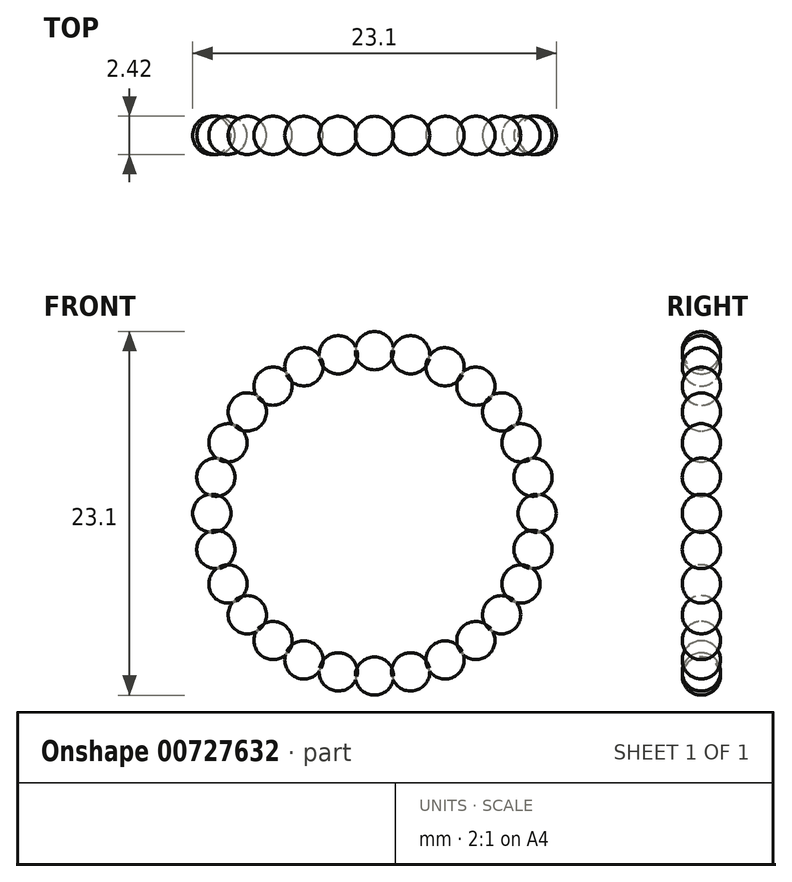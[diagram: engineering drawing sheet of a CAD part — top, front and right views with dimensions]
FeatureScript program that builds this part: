
annotation { "Feature Type Name" : "Feature", "Feature Type Description" : "" }
export const myFeature = defineFeature(function(context is Context, id is Id, definition is map)
    precondition{}
    {
        {
            var Q0;
            Q0=qCreatedBy(makeId("Front.planeOp"),FACE);
            var sketch = newSketch(context, id + "F0", { "sketchPlane" : qUnion([Q0])});
            skCircle(sketch, "E0", {"center": v(0, 0) * mm, "radius": 9.5 * mm});
            skCircle(sketch, "E1", {"center": v(10.33, 0) * mm, "radius": 1.21 * mm});
            skLineSegment(sketch, "E2", {"start": v(10.33, 2.28) * mm, "end": v(10.33, -2.1) * mm});
            skSolve(sketch);
        }
        {
            var Q0;
            {var subQ0=sQuery(id+"F0.wireOp",EDGE,"E2");var subQ1=sQuery(id+"F0.wireOp",EDGE,"E1");var subQ2=makeQuery(id+"F0.imprint","INTERSECT",VERTEX,{"disambiguationData":[OD(0.0)],"derivedFrom":[subQ1,subQ0]});Q0=makeQuery(id+"F0.imprint","IMPRINT",FACE,{"disambiguationData":[TD([[makeQuery(id+"F0.imprint","IMPRINT",EDGE,{"disambiguationData":[TD([[subQ2,1.0]])],"derivedFrom":subQ1}),1.0]])]});}
            var Q1;
            Q1=sQuery(id+"F0.wireOp",EDGE,"E2");
            revolve(context, id + "F1", {"surfaceOperationType" : NewSurfaceOperationType.NEW, "entities" : qUnion([Q0]), "axis" : qUnion([Q1]), "revolveType" : RevolveType.FULL});
        }
        {
            var Q0;
            Q0=makeQuery(id+"F1.opRevolve","SWEPT_BODY",BODY,{"disambiguationData":[OSD([sQuery(id+"F0.wireOp",EDGE,"E1"),sQuery(id+"F0.wireOp",EDGE,"E2")])]});
            var Q1;
            Q1=sQuery(id+"F0.wireOp",EDGE,"E0");
            circularPattern(context, id + "F2", {"entities" : qUnion([Q0]), "axis" : qUnion([Q1]), "angle" : 360 * degree, "instanceCount" : 28, "equalSpace" : true});
        }
    });
